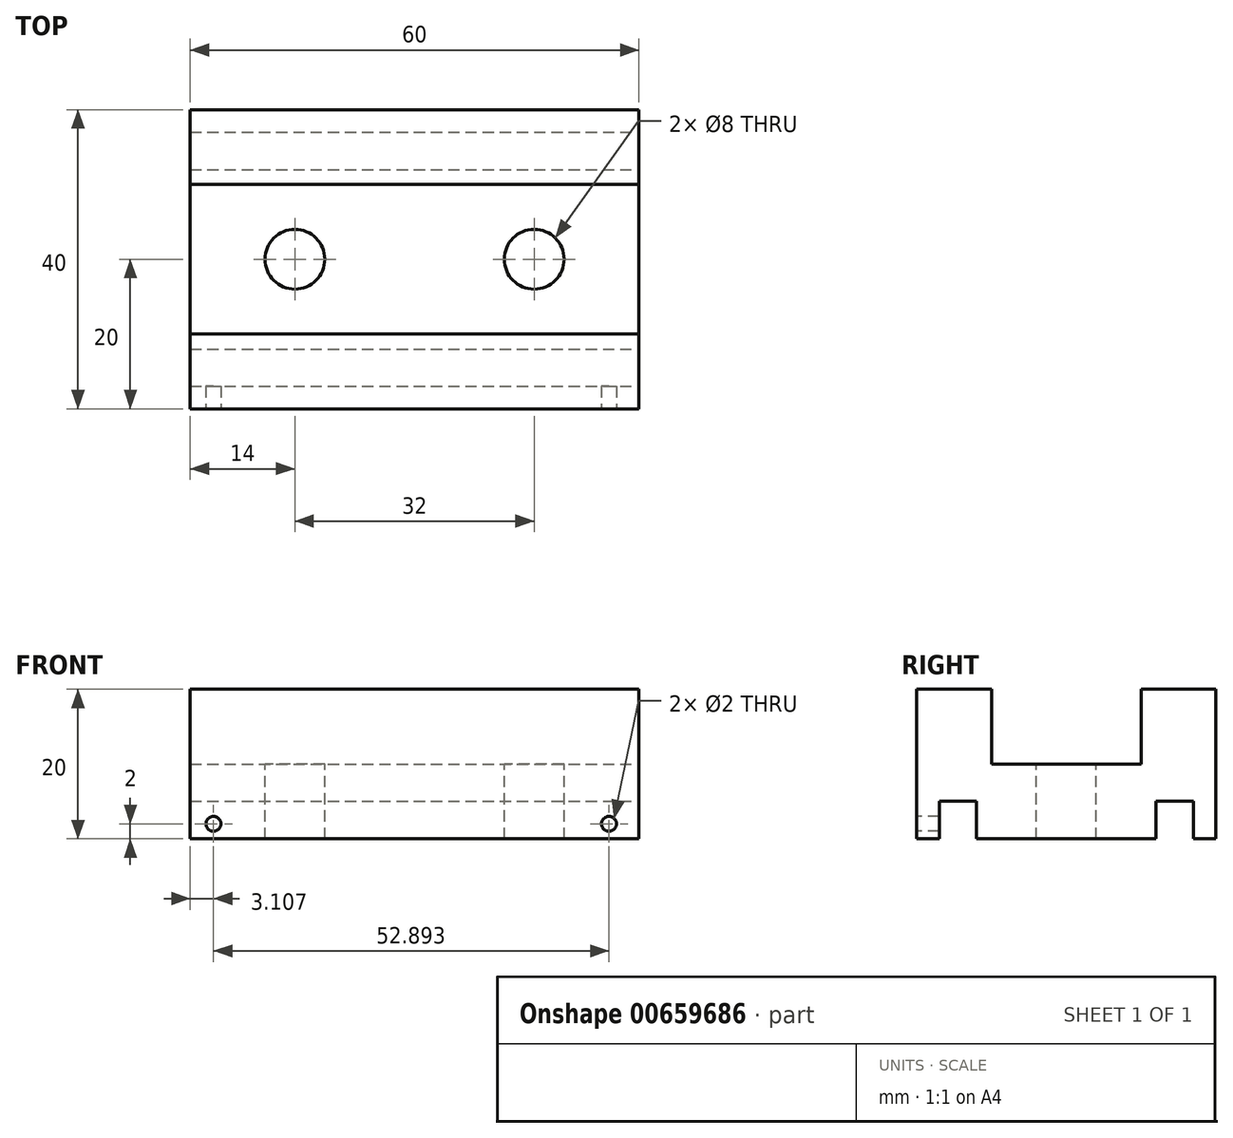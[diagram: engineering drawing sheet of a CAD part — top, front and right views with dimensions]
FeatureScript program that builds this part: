
annotation { "Feature Type Name" : "Feature", "Feature Type Description" : "" }
export const myFeature = defineFeature(function(context is Context, id is Id, definition is map)
    precondition{}
    {
        {
            var Q0;
            Q0=qCreatedBy(makeId("Top.planeOp"),FACE);
            var sketch = newSketch(context, id + "F0", { "sketchPlane" : qUnion([Q0])});
            skLineSegment(sketch, "E0.bottom", {"start": v(30, 20) * mm, "end": v(-30, 20) * mm});
            skLineSegment(sketch, "E0.top", {"start": v(30, -20) * mm, "end": v(-30, -20) * mm});
            skLineSegment(sketch, "E0.left", {"start": v(30, 20) * mm, "end": v(30, -20) * mm});
            skLineSegment(sketch, "E0.right", {"start": v(-30, 20) * mm, "end": v(-30, -20) * mm});
            skPoint(sketch, "E0.middle", {"position": v(0, 0) * mm});
            skSolve(sketch);
        }
        {
            var Q0;
            Q0=makeQuery(id+"F0.imprint","IMPRINT",FACE,{"disambiguationData":[TD([[makeQuery(id+"F0.imprint","IMPRINT",EDGE,{"derivedFrom":sQuery(id+"F0.wireOp",EDGE,"E0.bottom")}),1.0]])]});
            extrude(context, id + "F1", {"entities" : qUnion([Q0]), "depth" : 20 * mm, "offsetDistance" : 25 * mm});
        }
        {
            var Q0;
            Q0=makeQuery(id+"F1.opExtrude","CAP_FACE",FACE,{"disambiguationData":[OSD([sQuery(id+"F0.wireOp",EDGE,"E0.bottom"),sQuery(id+"F0.wireOp",EDGE,"E0.top"),sQuery(id+"F0.wireOp",EDGE,"E0.left"),sQuery(id+"F0.wireOp",EDGE,"E0.right")])],"isStart":false});
            var sketch = newSketch(context, id + "F2", { "sketchPlane" : qUnion([Q0])});
            skLineSegment(sketch, "E1.bottom", {"start": v(-30, 10) * mm, "end": v(30, 10) * mm});
            skLineSegment(sketch, "E1.top", {"start": v(-30, -10) * mm, "end": v(30, -10) * mm});
            skLineSegment(sketch, "E1.left", {"start": v(-30, 10) * mm, "end": v(-30, -10) * mm});
            skLineSegment(sketch, "E1.right", {"start": v(30, 10) * mm, "end": v(30, -10) * mm});
            skPoint(sketch, "E1.middle", {"position": v(0, 0) * mm});
            skSolve(sketch);
        }
        {
            var Q0;
            Q0=makeQuery(id+"F2.imprint","IMPRINT",FACE,{"disambiguationData":[TD([[makeQuery(id+"F2.imprint","IMPRINT",EDGE,{"derivedFrom":sQuery(id+"F2.wireOp",EDGE,"E1.bottom")}),-1.0]])]});
            extrude(context, id + "F3", {"entities" : qUnion([Q0]), "operationType" : NewBodyOperationType.REMOVE, "oppositeDirection" : true, "depth" : 10 * mm, "offsetDistance" : 25 * mm});
        }
        {
            var Q0;
            Q0=makeQuery(id+"F3.boolean.opBoolean","COPY",FACE,{"derivedFrom":makeQuery(id+"F3.opExtrude","CAP_FACE",FACE,{"disambiguationData":[OSD([sQuery(id+"F2.wireOp",EDGE,"E1.bottom"),sQuery(id+"F2.wireOp",EDGE,"E1.top"),sQuery(id+"F2.wireOp",EDGE,"E1.left"),sQuery(id+"F2.wireOp",EDGE,"E1.right")])],"isStart":false})});
            var sketch = newSketch(context, id + "F4", { "sketchPlane" : qUnion([Q0])});
            skCircle(sketch, "E2", {"center": v(-16, 0) * mm, "radius": 4 * mm});
            skCircle(sketch, "E3", {"center": v(16, 0) * mm, "radius": 4 * mm});
            skSolve(sketch);
        }
        {
            var Q0;
            Q0=makeQuery(id+"F4.imprint","IMPRINT",FACE,{"disambiguationData":[TD([[makeQuery(id+"F4.imprint","IMPRINT",EDGE,{"derivedFrom":sQuery(id+"F4.wireOp",EDGE,"E2")}),1.0]])]});
            extrude(context, id + "F5", {"entities" : qUnion([Q0]), "operationType" : NewBodyOperationType.REMOVE, "oppositeDirection" : true, "depth" : 25 * mm, "offsetDistance" : 25 * mm});
        }
        {
            var Q0;
            Q0=makeQuery(id+"F3.boolean.opBoolean","COPY",FACE,{"derivedFrom":makeQuery(id+"F3.opExtrude","CAP_FACE",FACE,{"disambiguationData":[OSD([sQuery(id+"F2.wireOp",EDGE,"E1.bottom"),sQuery(id+"F2.wireOp",EDGE,"E1.top"),sQuery(id+"F2.wireOp",EDGE,"E1.left"),sQuery(id+"F2.wireOp",EDGE,"E1.right")])],"isStart":false})});
            var sketch = newSketch(context, id + "F6", { "sketchPlane" : qUnion([Q0])});
            skCircle(sketch, "E4", {"center": v(16, 0) * mm, "radius": 4 * mm});
            skSolve(sketch);
        }
        {
            var Q0;
            Q0=makeQuery(id+"F6.imprint","IMPRINT",FACE,{"disambiguationData":[TD([[makeQuery(id+"F6.imprint","IMPRINT",EDGE,{"derivedFrom":sQuery(id+"F6.wireOp",EDGE,"E4")}),1.0]])]});
            extrude(context, id + "F7", {"entities" : qUnion([Q0]), "operationType" : NewBodyOperationType.REMOVE, "oppositeDirection" : true, "depth" : 25 * mm, "offsetDistance" : 25 * mm});
        }
        {
            var Q0;
            Q0=makeQuery(id+"F1.opExtrude","CAP_FACE",FACE,{"disambiguationData":[OSD([sQuery(id+"F0.wireOp",EDGE,"E0.bottom"),sQuery(id+"F0.wireOp",EDGE,"E0.top"),sQuery(id+"F0.wireOp",EDGE,"E0.left"),sQuery(id+"F0.wireOp",EDGE,"E0.right")])],"isStart":true});
            var sketch = newSketch(context, id + "F8", { "sketchPlane" : qUnion([Q0])});
            skLineSegment(sketch, "E5.bottom", {"start": v(-30, 17) * mm, "end": v(30, 17) * mm});
            skLineSegment(sketch, "E5.top", {"start": v(-30, 12) * mm, "end": v(30, 12) * mm});
            skLineSegment(sketch, "E5.left", {"start": v(-30, 17) * mm, "end": v(-30, 12) * mm});
            skLineSegment(sketch, "E5.right", {"start": v(30, 17) * mm, "end": v(30, 12) * mm});
            skSolve(sketch);
        }
        {
            var Q0;
            Q0=makeQuery(id+"F8.imprint","IMPRINT",FACE,{"disambiguationData":[TD([[makeQuery(id+"F8.imprint","IMPRINT",EDGE,{"derivedFrom":sQuery(id+"F8.wireOp",EDGE,"E5.bottom")}),-1.0]])]});
            extrude(context, id + "F9", {"entities" : qUnion([Q0]), "operationType" : NewBodyOperationType.REMOVE, "oppositeDirection" : true, "depth" : 5 * mm, "offsetDistance" : 25 * mm});
        }
        {
            var Q0;
            {var subQ0=sQuery(id+"F0.wireOp",EDGE,"E0.left");var subQ1=sQuery(id+"F0.wireOp",EDGE,"E0.right");var subQ2=sQuery(id+"F0.wireOp",EDGE,"E0.bottom");Q0=makeQuery(id+"F9.boolean.opBoolean","SPLIT",FACE,{"disambiguationData":[TD([makeQuery(id+"F1.opExtrude","SWEPT_FACE",FACE,{"disambiguationData":[OSD([subQ2])]})])],"derivedFrom":makeQuery(id+"F1.opExtrude","CAP_FACE",FACE,{"disambiguationData":[OSD([subQ2,sQuery(id+"F0.wireOp",EDGE,"E0.top"),subQ0,subQ1])],"isStart":true})});}
            var sketch = newSketch(context, id + "F10", { "sketchPlane" : qUnion([Q0])});
            skLineSegment(sketch, "E6.bottom", {"start": v(-30, -17) * mm, "end": v(30, -17) * mm});
            skLineSegment(sketch, "E6.top", {"start": v(-30, -12) * mm, "end": v(30, -12) * mm});
            skLineSegment(sketch, "E6.left", {"start": v(-30, -17) * mm, "end": v(-30, -12) * mm});
            skLineSegment(sketch, "E6.right", {"start": v(30, -17) * mm, "end": v(30, -12) * mm});
            skSolve(sketch);
        }
        {
            var Q0;
            Q0=makeQuery(id+"F10.imprint","IMPRINT",FACE,{"disambiguationData":[TD([[makeQuery(id+"F10.imprint","IMPRINT",EDGE,{"derivedFrom":sQuery(id+"F10.wireOp",EDGE,"E6.bottom")}),1.0]])]});
            extrude(context, id + "F11", {"entities" : qUnion([Q0]), "operationType" : NewBodyOperationType.REMOVE, "oppositeDirection" : true, "depth" : 5 * mm, "offsetDistance" : 25 * mm});
        }
        {
            var Q0;
            Q0=makeQuery(id+"F1.opExtrude","SWEPT_FACE",FACE,{"disambiguationData":[OSD([sQuery(id+"F0.wireOp",EDGE,"E0.top")])]});
            var sketch = newSketch(context, id + "F12", { "sketchPlane" : qUnion([Q0])});
            skCircle(sketch, "E7", {"center": v(-26.9, 2) * mm, "radius": 1 * mm});
            skSolve(sketch);
        }
        {
            var Q0;
            Q0=makeQuery(id+"F12.imprint","IMPRINT",FACE,{"disambiguationData":[TD([[makeQuery(id+"F12.imprint","IMPRINT",EDGE,{"derivedFrom":sQuery(id+"F12.wireOp",EDGE,"E7")}),1.0]])]});
            extrude(context, id + "F13", {"entities" : qUnion([Q0]), "operationType" : NewBodyOperationType.REMOVE, "oppositeDirection" : true, "depth" : 5 * mm, "offsetDistance" : 25 * mm});
        }
        {
            var Q0;
            Q0=makeQuery(id+"F1.opExtrude","SWEPT_FACE",FACE,{"disambiguationData":[OSD([sQuery(id+"F0.wireOp",EDGE,"E0.top")])]});
            var sketch = newSketch(context, id + "F14", { "sketchPlane" : qUnion([Q0])});
            skCircle(sketch, "E8", {"center": v(26, 2) * mm, "radius": 1 * mm});
            skSolve(sketch);
        }
        {
            var Q0;
            Q0=makeQuery(id+"F14.imprint","IMPRINT",FACE,{"disambiguationData":[TD([[makeQuery(id+"F14.imprint","IMPRINT",EDGE,{"derivedFrom":sQuery(id+"F14.wireOp",EDGE,"E8")}),1.0]])]});
            extrude(context, id + "F15", {"entities" : qUnion([Q0]), "operationType" : NewBodyOperationType.REMOVE, "oppositeDirection" : true, "depth" : 5 * mm, "offsetDistance" : 25 * mm});
        }
    });
